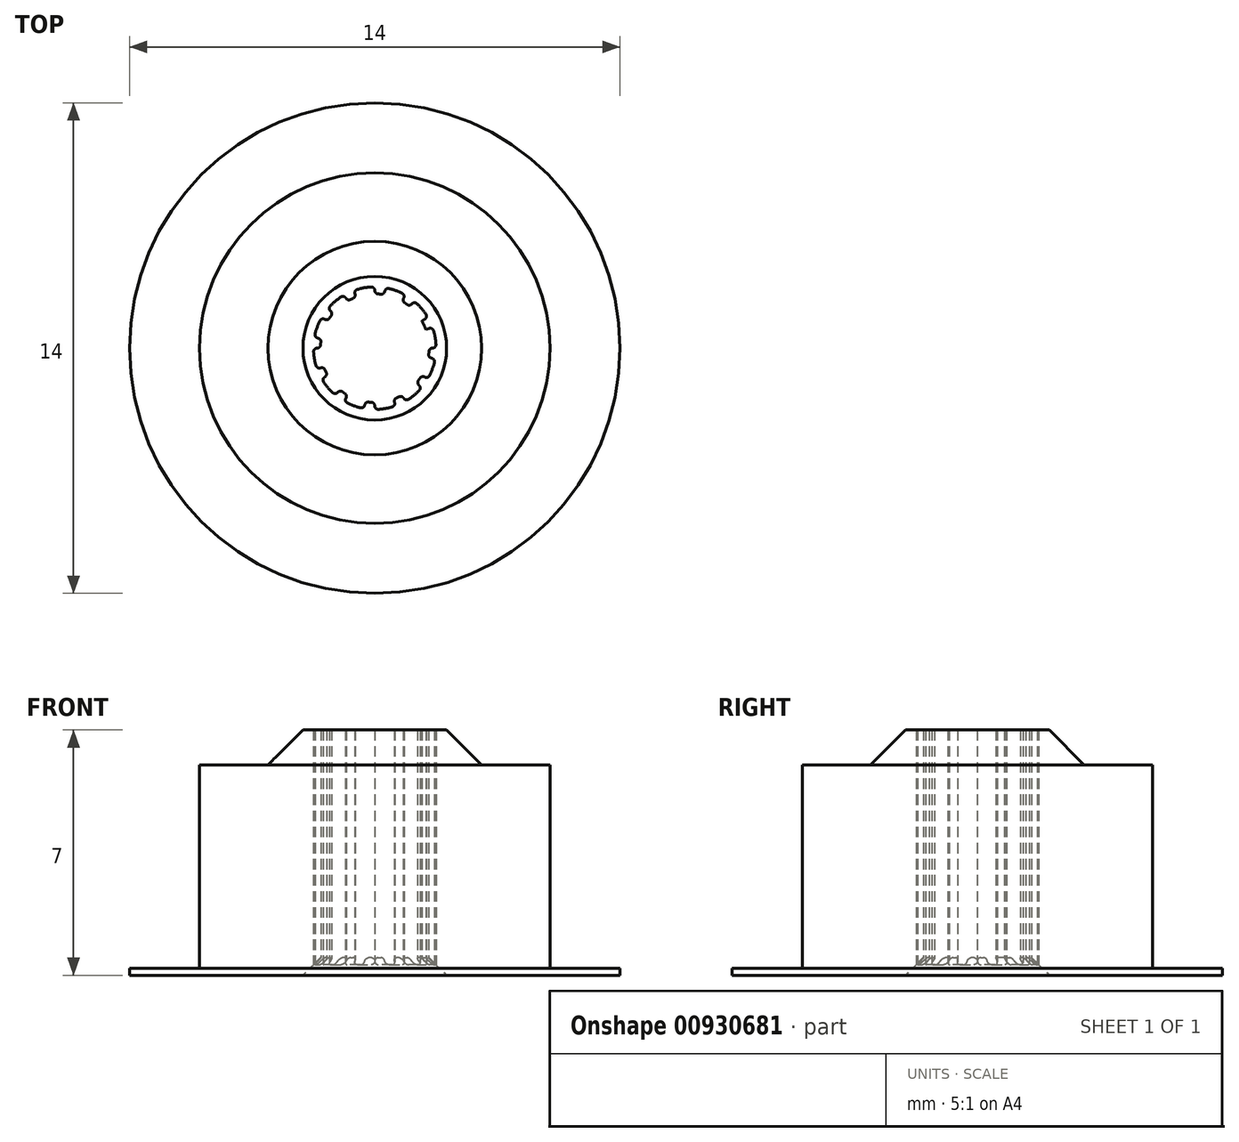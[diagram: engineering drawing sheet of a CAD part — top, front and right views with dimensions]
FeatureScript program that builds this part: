
annotation { "Feature Type Name" : "Feature", "Feature Type Description" : "" }
export const myFeature = defineFeature(function(context is Context, id is Id, definition is map)
    precondition{}
    {
        {
            var Q0;
            Q0=qCreatedBy(makeId("Front.planeOp"),FACE);
            var sketch = newSketch(context, id + "F0", { "sketchPlane" : qUnion([Q0])});
            skLineSegment(sketch, "E0", {"start": v(0, 0) * mm, "end": v(0, 10) * mm, "construction": true});
            skLineSegment(sketch, "E1", {"start": v(1.55, 7) * mm, "end": v(2.05, 7) * mm});
            skLineSegment(sketch, "E2", {"start": v(2.05, 7) * mm, "end": v(3.05, 6) * mm});
            skLineSegment(sketch, "E3", {"start": v(3.05, 6) * mm, "end": v(5, 6) * mm});
            skLineSegment(sketch, "E4", {"start": v(5, 6) * mm, "end": v(5, 0) * mm});
            skLineSegment(sketch, "E5", {"start": v(5, 0) * mm, "end": v(2.05, 0) * mm});
            skLineSegment(sketch, "E6", {"start": v(1.55, 0.5) * mm, "end": v(1.55, 7) * mm});
            skLineSegment(sketch, "E7", {"start": v(2.05, 0) * mm, "end": v(1.55, 0.5) * mm});
            skSolve(sketch);
        }
        {
            var Q0;
            Q0=qSketchRegion(id+"F0",true);
            var Q1;
            Q1=sQuery(id+"F0.wireOp",EDGE,"E0");
            revolve(context, id + "F1", {"entities" : qUnion([Q0]), "axis" : qUnion([Q1]), "revolveType" : RevolveType.FULL});
        }
        {
            var Q0;
            Q0=makeQuery(id+"F1.opRevolve","SWEPT_FACE",FACE,{"disambiguationData":[OSD([sQuery(id+"F0.wireOp",EDGE,"E5")])]});
            var sketch = newSketch(context, id + "F2", { "sketchPlane" : qUnion([Q0])});
            skCircle(sketch, "E8", {"center": v(0, 0) * mm, "radius": 1.5 * mm, "construction": true});
            skArc(sketch, "E9", {"start": v(-1.72, -0.3) * mm, "mid": v(-1.64, -0.6) * mm, "end": v(-1.52, -0.87) * mm});
            skArc(sketch, "E10", {"start": v(-1.34, -0.78) * mm, "mid": v(-1.27, -0.89) * mm, "end": v(-1.19, -1) * mm});
            skLineSegment(sketch, "E11", {"start": v(-1.75, 0) * mm, "end": v(-1.55, 0) * mm});
            skLineSegment(sketch, "E12", {"start": v(-1.72, -0.3) * mm, "end": v(-1.53, -0.27) * mm});
            skLineSegment(sketch, "E13.1.0", {"start": v(-1.34, -1.12) * mm, "end": v(-1.19, -1) * mm});
            skLineSegment(sketch, "E13.1.1", {"start": v(-1.52, -0.88) * mm, "end": v(-1.34, -0.78) * mm});
            skLineSegment(sketch, "E13.2.0", {"start": v(-0.6, -1.64) * mm, "end": v(-0.53, -1.46) * mm});
            skLineSegment(sketch, "E13.2.1", {"start": v(-0.88, -1.52) * mm, "end": v(-0.78, -1.34) * mm});
            skLineSegment(sketch, "E13.3.0", {"start": v(0.3, -1.72) * mm, "end": v(0.27, -1.53) * mm});
            skLineSegment(sketch, "E13.3.1", {"start": v(0, -1.75) * mm, "end": v(0, -1.55) * mm});
            skLineSegment(sketch, "E13.4.0", {"start": v(1.12, -1.34) * mm, "end": v(1, -1.19) * mm});
            skLineSegment(sketch, "E13.4.1", {"start": v(0.88, -1.52) * mm, "end": v(0.78, -1.34) * mm});
            skLineSegment(sketch, "E13.5.0", {"start": v(1.64, -0.6) * mm, "end": v(1.46, -0.53) * mm});
            skLineSegment(sketch, "E13.5.1", {"start": v(1.52, -0.88) * mm, "end": v(1.34, -0.78) * mm});
            skLineSegment(sketch, "E13.6.0", {"start": v(1.72, 0.3) * mm, "end": v(1.53, 0.27) * mm});
            skLineSegment(sketch, "E13.6.1", {"start": v(1.75, 0) * mm, "end": v(1.55, 0) * mm});
            skLineSegment(sketch, "E13.7.0", {"start": v(1.34, 1.12) * mm, "end": v(1.19, 1) * mm});
            skLineSegment(sketch, "E13.7.1", {"start": v(1.52, 0.88) * mm, "end": v(1.34, 0.78) * mm});
            skLineSegment(sketch, "E13.8.0", {"start": v(0.6, 1.64) * mm, "end": v(0.53, 1.46) * mm});
            skLineSegment(sketch, "E13.8.1", {"start": v(0.88, 1.52) * mm, "end": v(0.78, 1.34) * mm});
            skLineSegment(sketch, "E13.9.0", {"start": v(-0.3, 1.72) * mm, "end": v(-0.27, 1.53) * mm});
            skLineSegment(sketch, "E13.9.1", {"start": v(0, 1.75) * mm, "end": v(0, 1.55) * mm});
            skLineSegment(sketch, "E13.10.0", {"start": v(-1.12, 1.34) * mm, "end": v(-1, 1.19) * mm});
            skLineSegment(sketch, "E13.10.1", {"start": v(-0.87, 1.52) * mm, "end": v(-0.77, 1.34) * mm});
            skLineSegment(sketch, "E13.11.0", {"start": v(-1.64, 0.6) * mm, "end": v(-1.46, 0.53) * mm});
            skLineSegment(sketch, "E13.11.1", {"start": v(-1.52, 0.88) * mm, "end": v(-1.34, 0.78) * mm});
            skArc(sketch, "E14.trimOffspring", {"start": v(-1.34, -1.12) * mm, "mid": v(-1.12, -1.34) * mm, "end": v(-0.88, -1.52) * mm});
            skArc(sketch, "E15.trimOffspring", {"start": v(-0.6, -1.64) * mm, "mid": v(-0.3, -1.72) * mm, "end": v(0, -1.75) * mm});
            skArc(sketch, "E16.trimOffspring", {"start": v(0.3, -1.72) * mm, "mid": v(0.6, -1.64) * mm, "end": v(0.87, -1.52) * mm});
            skArc(sketch, "E17.trimOffspring", {"start": v(1.12, -1.34) * mm, "mid": v(1.34, -1.12) * mm, "end": v(1.52, -0.88) * mm});
            skArc(sketch, "E18.trimOffspring", {"start": v(1.64, -0.6) * mm, "mid": v(1.72, -0.3) * mm, "end": v(1.75, 0) * mm});
            skArc(sketch, "E19.trimOffspring", {"start": v(1.72, 0.3) * mm, "mid": v(1.64, 0.6) * mm, "end": v(1.52, 0.87) * mm});
            skArc(sketch, "E20.trimOffspring", {"start": v(1.34, 1.12) * mm, "mid": v(1.12, 1.34) * mm, "end": v(0.88, 1.52) * mm});
            skArc(sketch, "E21.trimOffspring", {"start": v(0.6, 1.64) * mm, "mid": v(0.3, 1.72) * mm, "end": v(0, 1.75) * mm});
            skArc(sketch, "E22.trimOffspring", {"start": v(-0.3, 1.72) * mm, "mid": v(-0.6, 1.64) * mm, "end": v(-0.87, 1.52) * mm});
            skArc(sketch, "E23.trimOffspring", {"start": v(-1.12, 1.34) * mm, "mid": v(-1.34, 1.12) * mm, "end": v(-1.52, 0.88) * mm});
            skArc(sketch, "E24.trimOffspring", {"start": v(-1.64, 0.6) * mm, "mid": v(-1.72, 0.3) * mm, "end": v(-1.75, 0) * mm});
            skArc(sketch, "E25.trimOffspring", {"start": v(-0.78, -1.34) * mm, "mid": v(-0.66, -1.4) * mm, "end": v(-0.53, -1.46) * mm});
            skArc(sketch, "E26.trimOffspring", {"start": v(0, -1.55) * mm, "mid": v(0.14, -1.54) * mm, "end": v(0.27, -1.53) * mm});
            skArc(sketch, "E27.trimOffspring", {"start": v(0.77, -1.34) * mm, "mid": v(0.89, -1.27) * mm, "end": v(1, -1.19) * mm});
            skArc(sketch, "E28.trimOffspring", {"start": v(1.34, -0.78) * mm, "mid": v(1.4, -0.66) * mm, "end": v(1.46, -0.53) * mm});
            skArc(sketch, "E29.trimOffspring", {"start": v(1.55, 0) * mm, "mid": v(1.54, 0.14) * mm, "end": v(1.53, 0.27) * mm});
            skArc(sketch, "E30.trimOffspring", {"start": v(1.34, 0.77) * mm, "mid": v(1.27, 0.89) * mm, "end": v(1.19, 1) * mm});
            skArc(sketch, "E31.trimOffspring", {"start": v(0.78, 1.34) * mm, "mid": v(0.66, 1.4) * mm, "end": v(0.53, 1.46) * mm});
            skArc(sketch, "E32.trimOffspring", {"start": v(0, 1.55) * mm, "mid": v(-0.14, 1.54) * mm, "end": v(-0.27, 1.53) * mm});
            skArc(sketch, "E33.trimOffspring", {"start": v(-0.77, 1.34) * mm, "mid": v(-0.89, 1.27) * mm, "end": v(-1, 1.19) * mm});
            skArc(sketch, "E34.trimOffspring", {"start": v(-1.34, 0.78) * mm, "mid": v(-1.4, 0.66) * mm, "end": v(-1.46, 0.53) * mm});
            skArc(sketch, "E35.trimOffspring", {"start": v(-1.55, 0) * mm, "mid": v(-1.54, -0.14) * mm, "end": v(-1.53, -0.27) * mm});
            skSolve(sketch);
        }
        {
            var Q0;
            Q0=qSketchRegion(id+"F2",true);
            var Q1;
            Q1=makeQuery(id+"F1.opRevolve","SWEPT_FACE",FACE,{"disambiguationData":[OSD([sQuery(id+"F0.wireOp",EDGE,"E1")])]});
            extrude(context, id + "F3", {"entities" : qUnion([Q0]), "operationType" : NewBodyOperationType.REMOVE, "endBound" : BoundingType.UP_TO_SURFACE, "oppositeDirection" : true, "depth" : 25 * mm, "endBoundEntityFace" : qUnion([Q1]), "offsetDistance" : 25 * mm});
        }
        {
            var Q0;
            Q0=makeQuery(id+"F3.boolean.opBoolean","COPY",EDGE,{"derivedFrom":makeQuery(id+"F3.opExtrude","SWEPT_EDGE",EDGE,{"disambiguationData":[OSD([sQuery(id+"F2.wireOp",EDGE,"E13.4.0"),sQuery(id+"F2.wireOp",EDGE,"E17.trimOffspring")])]})});
            var Q1;
            Q1=makeQuery(id+"F3.boolean.opBoolean","COPY",EDGE,{"derivedFrom":makeQuery(id+"F3.opExtrude","SWEPT_EDGE",EDGE,{"disambiguationData":[OSD([sQuery(id+"F2.wireOp",EDGE,"E13.4.1"),sQuery(id+"F2.wireOp",EDGE,"E16.trimOffspring")])]})});
            var Q2;
            Q2=makeQuery(id+"F3.boolean.opBoolean","COPY",EDGE,{"derivedFrom":makeQuery(id+"F3.opExtrude","SWEPT_EDGE",EDGE,{"disambiguationData":[OSD([sQuery(id+"F2.wireOp",EDGE,"E13.4.0"),sQuery(id+"F2.wireOp",EDGE,"E27.trimOffspring")])]})});
            var Q3;
            Q3=makeQuery(id+"F3.boolean.opBoolean","COPY",EDGE,{"derivedFrom":makeQuery(id+"F3.opExtrude","SWEPT_EDGE",EDGE,{"disambiguationData":[OSD([sQuery(id+"F2.wireOp",EDGE,"E13.4.1"),sQuery(id+"F2.wireOp",EDGE,"E27.trimOffspring")])]})});
            var Q4;
            Q4=makeQuery(id+"F3.boolean.opBoolean","COPY",EDGE,{"derivedFrom":makeQuery(id+"F3.opExtrude","SWEPT_EDGE",EDGE,{"disambiguationData":[OSD([sQuery(id+"F2.wireOp",EDGE,"E13.3.0"),sQuery(id+"F2.wireOp",EDGE,"E16.trimOffspring")])]})});
            var Q5;
            Q5=makeQuery(id+"F3.boolean.opBoolean","COPY",EDGE,{"derivedFrom":makeQuery(id+"F3.opExtrude","SWEPT_EDGE",EDGE,{"disambiguationData":[OSD([sQuery(id+"F2.wireOp",EDGE,"E13.3.0"),sQuery(id+"F2.wireOp",EDGE,"E26.trimOffspring")])]})});
            var Q6;
            Q6=makeQuery(id+"F3.boolean.opBoolean","COPY",EDGE,{"derivedFrom":makeQuery(id+"F3.opExtrude","SWEPT_EDGE",EDGE,{"disambiguationData":[OSD([sQuery(id+"F2.wireOp",EDGE,"E13.3.1"),sQuery(id+"F2.wireOp",EDGE,"E26.trimOffspring")])]})});
            var Q7;
            Q7=makeQuery(id+"F3.boolean.opBoolean","COPY",EDGE,{"derivedFrom":makeQuery(id+"F3.opExtrude","SWEPT_EDGE",EDGE,{"disambiguationData":[OSD([sQuery(id+"F2.wireOp",EDGE,"E13.3.1"),sQuery(id+"F2.wireOp",EDGE,"E15.trimOffspring")])]})});
            var Q8;
            Q8=makeQuery(id+"F3.boolean.opBoolean","COPY",EDGE,{"derivedFrom":makeQuery(id+"F3.opExtrude","SWEPT_EDGE",EDGE,{"disambiguationData":[OSD([sQuery(id+"F2.wireOp",EDGE,"E13.2.0"),sQuery(id+"F2.wireOp",EDGE,"E15.trimOffspring")])]})});
            var Q9;
            Q9=makeQuery(id+"F3.boolean.opBoolean","COPY",EDGE,{"derivedFrom":makeQuery(id+"F3.opExtrude","SWEPT_EDGE",EDGE,{"disambiguationData":[OSD([sQuery(id+"F2.wireOp",EDGE,"E13.2.0"),sQuery(id+"F2.wireOp",EDGE,"E25.trimOffspring")])]})});
            var Q10;
            Q10=makeQuery(id+"F3.boolean.opBoolean","COPY",EDGE,{"derivedFrom":makeQuery(id+"F3.opExtrude","SWEPT_EDGE",EDGE,{"disambiguationData":[OSD([sQuery(id+"F2.wireOp",EDGE,"E13.2.1"),sQuery(id+"F2.wireOp",EDGE,"E25.trimOffspring")])]})});
            var Q11;
            Q11=makeQuery(id+"F3.boolean.opBoolean","COPY",EDGE,{"derivedFrom":makeQuery(id+"F3.opExtrude","SWEPT_EDGE",EDGE,{"disambiguationData":[OSD([sQuery(id+"F2.wireOp",EDGE,"E13.2.1"),sQuery(id+"F2.wireOp",EDGE,"E14.trimOffspring")])]})});
            var Q12;
            Q12=makeQuery(id+"F3.boolean.opBoolean","COPY",EDGE,{"derivedFrom":makeQuery(id+"F3.opExtrude","SWEPT_EDGE",EDGE,{"disambiguationData":[OSD([sQuery(id+"F2.wireOp",EDGE,"E13.1.0"),sQuery(id+"F2.wireOp",EDGE,"E14.trimOffspring")])]})});
            var Q13;
            Q13=makeQuery(id+"F3.boolean.opBoolean","COPY",EDGE,{"derivedFrom":makeQuery(id+"F3.opExtrude","SWEPT_EDGE",EDGE,{"disambiguationData":[OSD([sQuery(id+"F2.wireOp",EDGE,"E10"),sQuery(id+"F2.wireOp",EDGE,"E13.1.0")])]})});
            var Q14;
            Q14=makeQuery(id+"F3.boolean.opBoolean","COPY",EDGE,{"derivedFrom":makeQuery(id+"F3.opExtrude","SWEPT_EDGE",EDGE,{"disambiguationData":[OSD([sQuery(id+"F2.wireOp",EDGE,"E10"),sQuery(id+"F2.wireOp",EDGE,"E13.1.1")])]})});
            var Q15;
            Q15=makeQuery(id+"F3.boolean.opBoolean","COPY",EDGE,{"derivedFrom":makeQuery(id+"F3.opExtrude","SWEPT_EDGE",EDGE,{"disambiguationData":[OSD([sQuery(id+"F2.wireOp",EDGE,"E9"),sQuery(id+"F2.wireOp",EDGE,"E13.1.1")])]})});
            var Q16;
            Q16=makeQuery(id+"F3.boolean.opBoolean","COPY",EDGE,{"derivedFrom":makeQuery(id+"F3.opExtrude","SWEPT_EDGE",EDGE,{"disambiguationData":[OSD([sQuery(id+"F2.wireOp",EDGE,"E9"),sQuery(id+"F2.wireOp",EDGE,"E12")])]})});
            var Q17;
            Q17=makeQuery(id+"F3.boolean.opBoolean","COPY",EDGE,{"derivedFrom":makeQuery(id+"F3.opExtrude","SWEPT_EDGE",EDGE,{"disambiguationData":[OSD([sQuery(id+"F2.wireOp",EDGE,"E12"),sQuery(id+"F2.wireOp",EDGE,"E35.trimOffspring")])]})});
            var Q18;
            Q18=makeQuery(id+"F3.boolean.opBoolean","COPY",EDGE,{"derivedFrom":makeQuery(id+"F3.opExtrude","SWEPT_EDGE",EDGE,{"disambiguationData":[OSD([sQuery(id+"F2.wireOp",EDGE,"E11"),sQuery(id+"F2.wireOp",EDGE,"E35.trimOffspring")])]})});
            var Q19;
            Q19=makeQuery(id+"F3.boolean.opBoolean","COPY",EDGE,{"derivedFrom":makeQuery(id+"F3.opExtrude","SWEPT_EDGE",EDGE,{"disambiguationData":[OSD([sQuery(id+"F2.wireOp",EDGE,"E11"),sQuery(id+"F2.wireOp",EDGE,"E24.trimOffspring")])]})});
            var Q20;
            Q20=makeQuery(id+"F3.boolean.opBoolean","COPY",EDGE,{"derivedFrom":makeQuery(id+"F3.opExtrude","SWEPT_EDGE",EDGE,{"disambiguationData":[OSD([sQuery(id+"F2.wireOp",EDGE,"E13.11.0"),sQuery(id+"F2.wireOp",EDGE,"E24.trimOffspring")])]})});
            var Q21;
            Q21=makeQuery(id+"F3.boolean.opBoolean","COPY",EDGE,{"derivedFrom":makeQuery(id+"F3.opExtrude","SWEPT_EDGE",EDGE,{"disambiguationData":[OSD([sQuery(id+"F2.wireOp",EDGE,"E13.11.0"),sQuery(id+"F2.wireOp",EDGE,"E34.trimOffspring")])]})});
            var Q22;
            Q22=makeQuery(id+"F3.boolean.opBoolean","COPY",EDGE,{"derivedFrom":makeQuery(id+"F3.opExtrude","SWEPT_EDGE",EDGE,{"disambiguationData":[OSD([sQuery(id+"F2.wireOp",EDGE,"E13.11.1"),sQuery(id+"F2.wireOp",EDGE,"E34.trimOffspring")])]})});
            var Q23;
            Q23=makeQuery(id+"F3.boolean.opBoolean","COPY",EDGE,{"derivedFrom":makeQuery(id+"F3.opExtrude","SWEPT_EDGE",EDGE,{"disambiguationData":[OSD([sQuery(id+"F2.wireOp",EDGE,"E13.11.1"),sQuery(id+"F2.wireOp",EDGE,"E23.trimOffspring")])]})});
            var Q24;
            Q24=makeQuery(id+"F3.boolean.opBoolean","COPY",EDGE,{"derivedFrom":makeQuery(id+"F3.opExtrude","SWEPT_EDGE",EDGE,{"disambiguationData":[OSD([sQuery(id+"F2.wireOp",EDGE,"E13.10.0"),sQuery(id+"F2.wireOp",EDGE,"E23.trimOffspring")])]})});
            var Q25;
            Q25=makeQuery(id+"F3.boolean.opBoolean","COPY",EDGE,{"derivedFrom":makeQuery(id+"F3.opExtrude","SWEPT_EDGE",EDGE,{"disambiguationData":[OSD([sQuery(id+"F2.wireOp",EDGE,"E13.10.0"),sQuery(id+"F2.wireOp",EDGE,"E33.trimOffspring")])]})});
            var Q26;
            Q26=makeQuery(id+"F3.boolean.opBoolean","COPY",EDGE,{"derivedFrom":makeQuery(id+"F3.opExtrude","SWEPT_EDGE",EDGE,{"disambiguationData":[OSD([sQuery(id+"F2.wireOp",EDGE,"E13.10.1"),sQuery(id+"F2.wireOp",EDGE,"E33.trimOffspring")])]})});
            var Q27;
            Q27=makeQuery(id+"F3.boolean.opBoolean","COPY",EDGE,{"derivedFrom":makeQuery(id+"F3.opExtrude","SWEPT_EDGE",EDGE,{"disambiguationData":[OSD([sQuery(id+"F2.wireOp",EDGE,"E13.10.1"),sQuery(id+"F2.wireOp",EDGE,"E22.trimOffspring")])]})});
            var Q28;
            Q28=makeQuery(id+"F3.boolean.opBoolean","COPY",EDGE,{"derivedFrom":makeQuery(id+"F3.opExtrude","SWEPT_EDGE",EDGE,{"disambiguationData":[OSD([sQuery(id+"F2.wireOp",EDGE,"E13.9.0"),sQuery(id+"F2.wireOp",EDGE,"E22.trimOffspring")])]})});
            var Q29;
            Q29=makeQuery(id+"F3.boolean.opBoolean","COPY",EDGE,{"derivedFrom":makeQuery(id+"F3.opExtrude","SWEPT_EDGE",EDGE,{"disambiguationData":[OSD([sQuery(id+"F2.wireOp",EDGE,"E13.9.0"),sQuery(id+"F2.wireOp",EDGE,"E32.trimOffspring")])]})});
            var Q30;
            Q30=makeQuery(id+"F3.boolean.opBoolean","COPY",EDGE,{"derivedFrom":makeQuery(id+"F3.opExtrude","SWEPT_EDGE",EDGE,{"disambiguationData":[OSD([sQuery(id+"F2.wireOp",EDGE,"E13.9.1"),sQuery(id+"F2.wireOp",EDGE,"E32.trimOffspring")])]})});
            var Q31;
            Q31=makeQuery(id+"F3.boolean.opBoolean","COPY",EDGE,{"derivedFrom":makeQuery(id+"F3.opExtrude","SWEPT_EDGE",EDGE,{"disambiguationData":[OSD([sQuery(id+"F2.wireOp",EDGE,"E13.9.1"),sQuery(id+"F2.wireOp",EDGE,"E21.trimOffspring")])]})});
            var Q32;
            Q32=makeQuery(id+"F3.boolean.opBoolean","COPY",EDGE,{"derivedFrom":makeQuery(id+"F3.opExtrude","SWEPT_EDGE",EDGE,{"disambiguationData":[OSD([sQuery(id+"F2.wireOp",EDGE,"E13.8.0"),sQuery(id+"F2.wireOp",EDGE,"E21.trimOffspring")])]})});
            var Q33;
            Q33=makeQuery(id+"F3.boolean.opBoolean","COPY",EDGE,{"derivedFrom":makeQuery(id+"F3.opExtrude","SWEPT_EDGE",EDGE,{"disambiguationData":[OSD([sQuery(id+"F2.wireOp",EDGE,"E13.8.0"),sQuery(id+"F2.wireOp",EDGE,"E31.trimOffspring")])]})});
            var Q34;
            Q34=makeQuery(id+"F3.boolean.opBoolean","COPY",EDGE,{"derivedFrom":makeQuery(id+"F3.opExtrude","SWEPT_EDGE",EDGE,{"disambiguationData":[OSD([sQuery(id+"F2.wireOp",EDGE,"E13.8.1"),sQuery(id+"F2.wireOp",EDGE,"E31.trimOffspring")])]})});
            var Q35;
            Q35=makeQuery(id+"F3.boolean.opBoolean","COPY",EDGE,{"derivedFrom":makeQuery(id+"F3.opExtrude","SWEPT_EDGE",EDGE,{"disambiguationData":[OSD([sQuery(id+"F2.wireOp",EDGE,"E13.8.1"),sQuery(id+"F2.wireOp",EDGE,"E20.trimOffspring")])]})});
            var Q36;
            Q36=makeQuery(id+"F3.boolean.opBoolean","COPY",EDGE,{"derivedFrom":makeQuery(id+"F3.opExtrude","SWEPT_EDGE",EDGE,{"disambiguationData":[OSD([sQuery(id+"F2.wireOp",EDGE,"E13.7.0"),sQuery(id+"F2.wireOp",EDGE,"E20.trimOffspring")])]})});
            var Q37;
            Q37=makeQuery(id+"F3.boolean.opBoolean","COPY",EDGE,{"derivedFrom":makeQuery(id+"F3.opExtrude","SWEPT_EDGE",EDGE,{"disambiguationData":[OSD([sQuery(id+"F2.wireOp",EDGE,"E13.7.0"),sQuery(id+"F2.wireOp",EDGE,"E30.trimOffspring")])]})});
            var Q38;
            Q38=makeQuery(id+"F3.boolean.opBoolean","COPY",EDGE,{"derivedFrom":makeQuery(id+"F3.opExtrude","SWEPT_EDGE",EDGE,{"disambiguationData":[OSD([sQuery(id+"F2.wireOp",EDGE,"E13.7.1"),sQuery(id+"F2.wireOp",EDGE,"E30.trimOffspring")])]})});
            var Q39;
            Q39=makeQuery(id+"F3.boolean.opBoolean","COPY",EDGE,{"derivedFrom":makeQuery(id+"F3.opExtrude","SWEPT_EDGE",EDGE,{"disambiguationData":[OSD([sQuery(id+"F2.wireOp",EDGE,"E13.7.1"),sQuery(id+"F2.wireOp",EDGE,"E19.trimOffspring")])]})});
            var Q40;
            Q40=makeQuery(id+"F3.boolean.opBoolean","COPY",EDGE,{"derivedFrom":makeQuery(id+"F3.opExtrude","SWEPT_EDGE",EDGE,{"disambiguationData":[OSD([sQuery(id+"F2.wireOp",EDGE,"E13.6.0"),sQuery(id+"F2.wireOp",EDGE,"E19.trimOffspring")])]})});
            var Q41;
            Q41=makeQuery(id+"F3.boolean.opBoolean","COPY",EDGE,{"derivedFrom":makeQuery(id+"F3.opExtrude","SWEPT_EDGE",EDGE,{"disambiguationData":[OSD([sQuery(id+"F2.wireOp",EDGE,"E13.6.0"),sQuery(id+"F2.wireOp",EDGE,"E29.trimOffspring")])]})});
            var Q42;
            Q42=makeQuery(id+"F3.boolean.opBoolean","COPY",EDGE,{"derivedFrom":makeQuery(id+"F3.opExtrude","SWEPT_EDGE",EDGE,{"disambiguationData":[OSD([sQuery(id+"F2.wireOp",EDGE,"E13.6.1"),sQuery(id+"F2.wireOp",EDGE,"E29.trimOffspring")])]})});
            var Q43;
            Q43=makeQuery(id+"F3.boolean.opBoolean","COPY",EDGE,{"derivedFrom":makeQuery(id+"F3.opExtrude","SWEPT_EDGE",EDGE,{"disambiguationData":[OSD([sQuery(id+"F2.wireOp",EDGE,"E13.6.1"),sQuery(id+"F2.wireOp",EDGE,"E18.trimOffspring")])]})});
            var Q44;
            Q44=makeQuery(id+"F3.boolean.opBoolean","COPY",EDGE,{"derivedFrom":makeQuery(id+"F3.opExtrude","SWEPT_EDGE",EDGE,{"disambiguationData":[OSD([sQuery(id+"F2.wireOp",EDGE,"E13.5.0"),sQuery(id+"F2.wireOp",EDGE,"E18.trimOffspring")])]})});
            var Q45;
            Q45=makeQuery(id+"F3.boolean.opBoolean","COPY",EDGE,{"derivedFrom":makeQuery(id+"F3.opExtrude","SWEPT_EDGE",EDGE,{"disambiguationData":[OSD([sQuery(id+"F2.wireOp",EDGE,"E13.5.0"),sQuery(id+"F2.wireOp",EDGE,"E28.trimOffspring")])]})});
            var Q46;
            Q46=makeQuery(id+"F3.boolean.opBoolean","COPY",EDGE,{"derivedFrom":makeQuery(id+"F3.opExtrude","SWEPT_EDGE",EDGE,{"disambiguationData":[OSD([sQuery(id+"F2.wireOp",EDGE,"E13.5.1"),sQuery(id+"F2.wireOp",EDGE,"E28.trimOffspring")])]})});
            var Q47;
            Q47=makeQuery(id+"F3.boolean.opBoolean","COPY",EDGE,{"derivedFrom":makeQuery(id+"F3.opExtrude","SWEPT_EDGE",EDGE,{"disambiguationData":[OSD([sQuery(id+"F2.wireOp",EDGE,"E13.5.1"),sQuery(id+"F2.wireOp",EDGE,"E17.trimOffspring")])]})});
            fillet(context, id + "F4", {"entities" : qUnion([Q0, Q1, Q2, Q3, Q4, Q5, Q6, Q7, Q8, Q9, Q10, Q11, Q12, Q13, Q14, Q15, Q16, Q17, Q18, Q19, Q20, Q21, Q22, Q23, Q24, Q25, Q26, Q27, Q28, Q29, Q30, Q31, Q32, Q33, Q34, Q35, Q36, Q37, Q38, Q39, Q40, Q41, Q42, Q43, Q44, Q45, Q46, Q47]), "radius" : 0.1 * mm, "tangentPropagation" : true, "allowEdgeOverflow" : false});
        }
        {
            var Q0;
            Q0=makeQuery(id+"F1.opRevolve","SWEPT_FACE",FACE,{"disambiguationData":[OSD([sQuery(id+"F0.wireOp",EDGE,"E5")])]});
            var sketch = newSketch(context, id + "F5", { "sketchPlane" : qUnion([Q0])});
            skCircle(sketch, "E36", {"center": v(0, 0) * mm, "radius": 7 * mm});
            skCircle(sketch, "E37", {"center": v(0, 0) * mm, "radius": 5 * mm});
            skSolve(sketch);
        }
        {
            var Q0;
            Q0=qSketchRegion(id+"F5",true);
            extrude(context, id + "F6", {"entities" : qUnion([Q0]), "operationType" : NewBodyOperationType.ADD, "oppositeDirection" : true, "depth" : 0.2 * mm, "offsetDistance" : 25 * mm});
        }
    });
